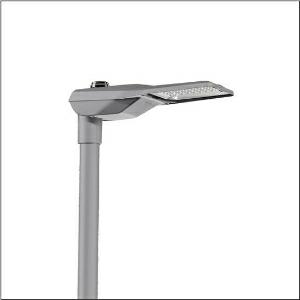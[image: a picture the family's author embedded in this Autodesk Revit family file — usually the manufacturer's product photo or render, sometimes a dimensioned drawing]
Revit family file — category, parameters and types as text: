
# Revit family: streetlight_sl_21_mini___st1_0a_5xe6d57n08jb_a4a3
name_source: partatom
category: Lighting Fixtures
units: mm (PartAtom-declared; Revit-internal decimal feet)

## family parameters
Cut with Voids When Loaded = No
Host = Face
Light Source = No
Part Type = Normal
Room Calculation Point = No
Round Connector Dimension = Use Diameter
Shared = No

## types (1)
- --- (1 x LED, 11030 lm, 87.3 W, 3000K)
    Apparent Load = 87 VA
    CIE Flux Codes = 40 73 97 100 100
    Color Rendering = 80
    Color Temperature = 3000K
    Default Elevation = 1800 mm
    Description = Streetlight SL 21 mini, mast luminaire, primary light control with lens, of PMMA, primary optical cover: cover, of toughened safety glass, transparent, light distribution: ST1.0a, light emission: direct distribution, primary light characteristic: asymmetric, installation type: side-entry, LED, 3G 2.5mm², High Power LED, rated luminous flux: 11.030lm, luminous efficacy: 126lm/W, light colour: 830, colour temperature: 3000K, control gear: NEMA (7pin), control: overheat protection, pre-setting: linear dimming characteristic, constant luminous flux control, time-dependent luminous flux control, flexible luminous flux parameterisation, mains connection: 230..240V, AC, 50/60Hz, connection cable pre-assembled, cable length: 10,5m, wiring characteristics: H05VV-F, start of lifetime: 87W, end of service life: 90W, reduction: 40W, luminaire housing, of diecast aluminium (EN AC-44300), powder-coated, Siteco® metallic grey (DB 702S), corrosivity category C5 mid according to DIN EN ISO 12944, multi-level sealing system, sealing non-destructively replaceable, inclination adjustable: 0°, 5°, 10°, 15°, length: 628mm, width: 235mm, height: 110mm, spigot size: 42mm (side-entry), mounting height: 4..8m, protection rating (complete): IP66, insulation class (complete): insulation class I (protective earthing), certification: CE, ENEC, ENEC+, VDE, impact resistance: IK10, permissible operating ambient temperature for outdoor applications: -40..+50°C, standard-compliant lighting for roads and squares, packaging unit: 1 piece

Light Distribution: ST1.0a
    Height = 110 mm
    Lamp = 1 x LED
    Lamp Light Flux = 11030 lm
    Lamp Power = 87.3 W
    Lamp count = 1
    Length = 625 mm
    Luminous efficacy = 126 lm/W
    Manufacturer = Siteco
    ModVariant = No
    Model = 5XE6D57N08JB
    Number of Poles = 1
    OnlyDefault = Yes
    Power Factor = 1
    Product Name = Streetlight SL 21 mini | ST1.0a
    Product group = mast luminaire | pylon top
    ProductGroupID = 6100
    Protection Class = Protection class I
    Protection Degree = IP 66
    RLX_Detail_Level = 1
    RLX_Emergency_Light_Flux = 0 lm
    RLX_Emergency_Type = 0
    RLX_Emergency_Type_DB = No
    RlxData = <blob elided: 25973 chars, md5=1cb20166>
    Socket = socket
    Standby Power = 0 W
    System Light Flux = 11030 lm
    System Power = 87 W
    Type Comments = factory setting: luminous flux: 100 % | dim-lin: 254 | 915 mA
    Type Image = l_1294379.jpg
    URL = http://relux.com
    VarID = @adj_156761
    Voltage = 0 V
    Weight = 0.00 kg
    Width = 234 mm

## geometry (parser evidence)
native form markers: Blend x4, Sweep x12
no freeform markers — native parametric forms only
